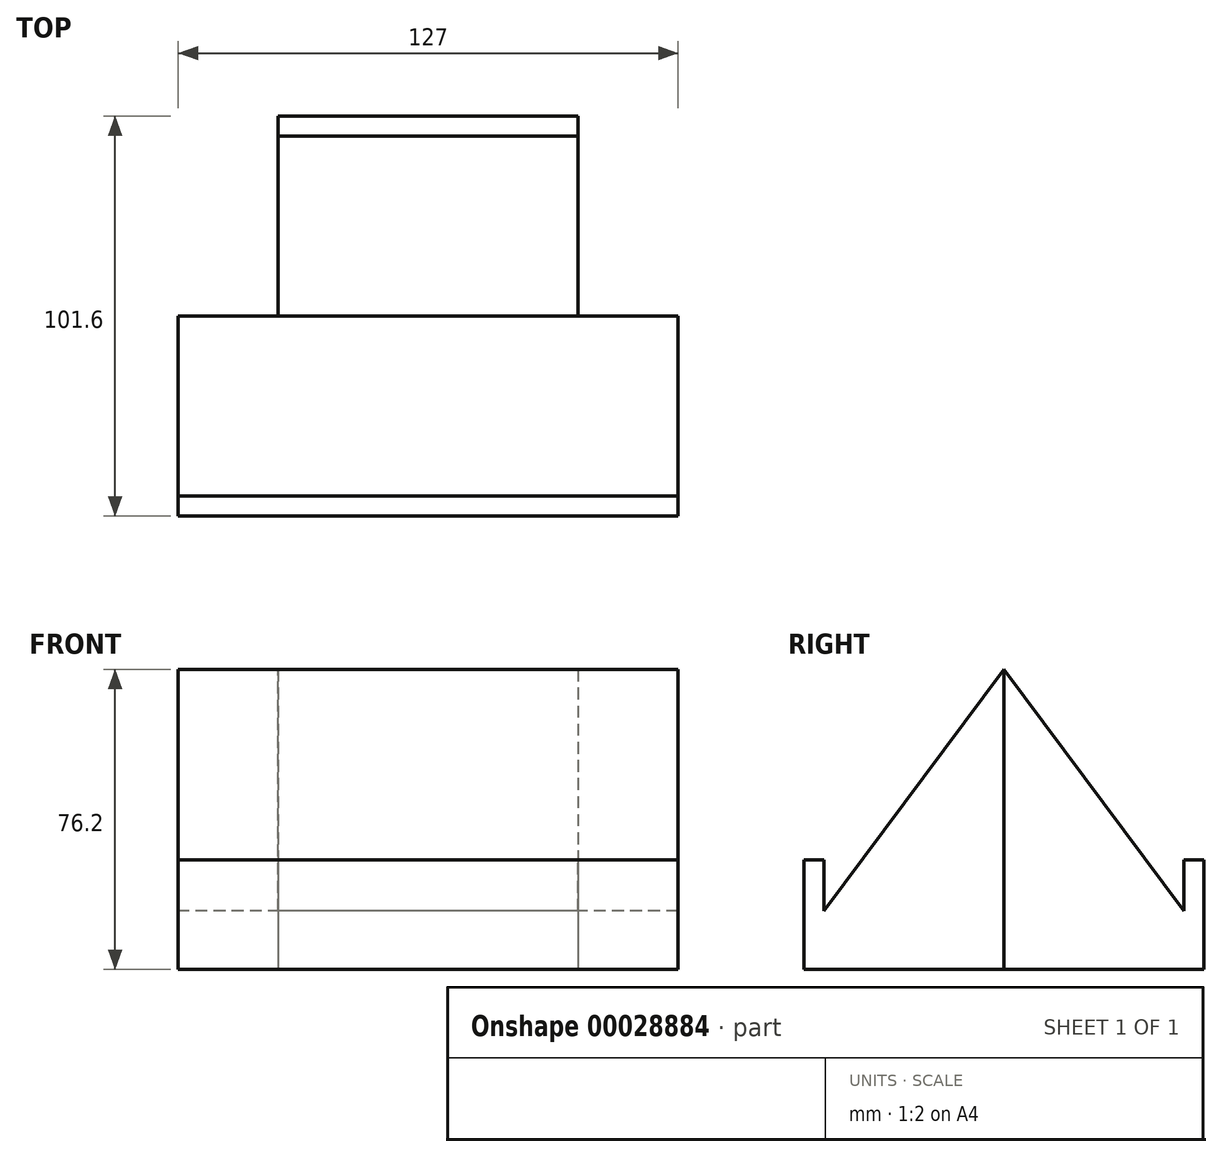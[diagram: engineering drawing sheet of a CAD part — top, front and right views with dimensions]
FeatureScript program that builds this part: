
annotation { "Feature Type Name" : "Feature", "Feature Type Description" : "" }
export const myFeature = defineFeature(function(context is Context, id is Id, definition is map)
    precondition{}
    {
        {
            var Q0;
            Q0=qCreatedBy(makeId("Front.planeOp"),FACE);
            var sketch = newSketch(context, id + "F0", { "sketchPlane" : qUnion([Q0])});
            skLineSegment(sketch, "E0.bottom", {"start": v(-63.5, 32.59) * mm, "end": v(63.5, 32.59) * mm});
            skLineSegment(sketch, "E0.top", {"start": v(-63.5, -43.61) * mm, "end": v(63.5, -43.61) * mm});
            skLineSegment(sketch, "E0.left", {"start": v(-63.5, 32.59) * mm, "end": v(-63.5, -43.61) * mm});
            skLineSegment(sketch, "E0.right", {"start": v(63.5, 32.59) * mm, "end": v(63.5, -43.61) * mm});
            skSolve(sketch);
        }
        {
            var Q0;
            Q0 = qSketchRegion(id + "F0", true);
            extrude(context, id + "F1", {"entities" : qUnion([Q0]), "oppositeDirection" : true, "depth" : 25.4 * mm});
        }
        {
            var Q0;
            Q0=makeQuery(id+"F1.opExtrude","CAP_FACE",FACE,{"disambiguationData":[OSD([sQuery(id+"F0.wireOp",EDGE,"E0.bottom"),sQuery(id+"F0.wireOp",EDGE,"E0.top"),sQuery(id+"F0.wireOp",EDGE,"E0.left"),sQuery(id+"F0.wireOp",EDGE,"E0.right")])],"isStart":true});
            extrude(context, id + "F2", {"entities" : qUnion([Q0]), "operationType" : NewBodyOperationType.ADD, "depth" : 25.4 * mm});
        }
        {
            var Q0;
            Q0=makeQuery(id+"F2.opExtrude","CAP_FACE",FACE,{"disambiguationData":[OSD([sQuery(id+"F0.wireOp",EDGE,"E0.bottom"),sQuery(id+"F0.wireOp",EDGE,"E0.top"),sQuery(id+"F0.wireOp",EDGE,"E0.left"),sQuery(id+"F0.wireOp",EDGE,"E0.right")])],"isStart":false});
            var sketch = newSketch(context, id + "F3", { "sketchPlane" : qUnion([Q0])});
            skLineSegment(sketch, "E1.bottom", {"start": v(-63.5, 32.59) * mm, "end": v(63.5, 32.59) * mm});
            skLineSegment(sketch, "E1.top", {"start": v(-63.5, -22.16) * mm, "end": v(63.5, -22.16) * mm});
            skLineSegment(sketch, "E1.left", {"start": v(-63.5, 32.59) * mm, "end": v(-63.5, -22.16) * mm});
            skLineSegment(sketch, "E1.right", {"start": v(63.5, 32.59) * mm, "end": v(63.5, -22.16) * mm});
            skSolve(sketch);
        }
        {
            var Q0;
            Q0 = qSketchRegion(id + "F3", true);
            extrude(context, id + "F4", {"entities" : qUnion([Q0]), "operationType" : NewBodyOperationType.REMOVE, "oppositeDirection" : true, "depth" : 5.08 * mm});
        }
        {
            var Q0;
            {var subQ0=sQuery(id+"F0.wireOp",EDGE,"E0.left");Q0=makeQuery(id+"F2.boolean.opBoolean","MERGE",FACE,{"derivedFrom":[makeQuery(id+"F1.opExtrude","SWEPT_FACE",FACE,{"disambiguationData":[OSD([subQ0])]}),makeQuery(id+"F2.opExtrude","SWEPT_FACE",FACE,{"disambiguationData":[OSD([subQ0])]})]});}
            var sketch = newSketch(context, id + "F5", { "sketchPlane" : qUnion([Q0])});
            skLineSegment(sketch, "E2", {"start": v(-25.4, 32.59) * mm, "end": v(20.32, 32.59) * mm});
            skLineSegment(sketch, "E3", {"start": v(20.32, 32.59) * mm, "end": v(20.32, -28.71) * mm});
            skLineSegment(sketch, "E4", {"start": v(20.32, -28.71) * mm, "end": v(-25.4, 32.59) * mm});
            skSolve(sketch);
        }
        {
            var Q0;
            Q0 = qSketchRegion(id + "F5", true);
            extrude(context, id + "F6", {"entities" : qUnion([Q0]), "operationType" : NewBodyOperationType.REMOVE, "oppositeDirection" : true, "depth" : 129.54 * mm});
        }
        {
            var Q0;
            Q0=makeQuery(id+"F4.boolean.opBoolean","COPY",FACE,{"derivedFrom":makeQuery(id+"F4.opExtrude","SWEPT_FACE",FACE,{"disambiguationData":[OSD([sQuery(id+"F3.wireOp",EDGE,"E1.top")])]})});
            extrude(context, id + "F7", {"entities" : qUnion([Q0]), "operationType" : NewBodyOperationType.ADD, "depth" : 6.35 * mm});
        }
        {
            var Q0;
            Q0=makeQuery(id+"F1.opExtrude","SWEPT_BODY",BODY,{"disambiguationData":[OSD([sQuery(id+"F0.wireOp",EDGE,"E0.bottom"),sQuery(id+"F0.wireOp",EDGE,"E0.top"),sQuery(id+"F0.wireOp",EDGE,"E0.left"),sQuery(id+"F0.wireOp",EDGE,"E0.right")])]});
            var Q1;
            Q1=makeQuery(id+"F1.opExtrude","CAP_FACE",FACE,{"disambiguationData":[OSD([sQuery(id+"F0.wireOp",EDGE,"E0.bottom"),sQuery(id+"F0.wireOp",EDGE,"E0.top"),sQuery(id+"F0.wireOp",EDGE,"E0.left"),sQuery(id+"F0.wireOp",EDGE,"E0.right")])],"isStart":false});
            mirror(context, id + "F8", {"operationType" : NewBodyOperationType.ADD, "entities" : qUnion([Q0]), "mirrorPlane" : qUnion([Q1])});
        }
        {
            var Q0;
            {var subQ0=sQuery(id+"F0.wireOp",EDGE,"E0.right");var subQ1=makeQuery(id+"F7.boolean.opBoolean","MERGE",FACE,{"derivedFrom":[makeQuery(id+"F2.boolean.opBoolean","MERGE",FACE,{"derivedFrom":[makeQuery(id+"F1.opExtrude","SWEPT_FACE",FACE,{"disambiguationData":[OSD([subQ0])]}),makeQuery(id+"F2.opExtrude","SWEPT_FACE",FACE,{"disambiguationData":[OSD([subQ0])]})]}),makeQuery(id+"F7.opExtrude","SWEPT_FACE",FACE,{"disambiguationData":[OSD([subQ0,sQuery(id+"F3.wireOp",EDGE,"E1.top"),sQuery(id+"F3.wireOp",EDGE,"E1.right")])]})]});Q0=makeQuery(id+"F8.boolean.opBoolean","MERGE",FACE,{"derivedFrom":[subQ1,makeQuery(id+"F8.opPattern","COPY",FACE,{"derivedFrom":subQ1,"instanceName":"1"})]});}
            var sketch = newSketch(context, id + "F9", { "sketchPlane" : qUnion([Q0])});
            skLineSegment(sketch, "E5.bottom", {"start": v(25.4, 32.59) * mm, "end": v(76.2, 32.59) * mm});
            skLineSegment(sketch, "E5.top", {"start": v(25.4, -43.61) * mm, "end": v(76.2, -43.61) * mm});
            skLineSegment(sketch, "E5.left", {"start": v(25.4, 32.59) * mm, "end": v(25.4, -43.61) * mm});
            skLineSegment(sketch, "E5.right", {"start": v(76.2, 32.59) * mm, "end": v(76.2, -43.61) * mm});
            skSolve(sketch);
        }
        {
            var Q0;
            Q0 = qSketchRegion(id + "F9", true);
            extrude(context, id + "F10", {"entities" : qUnion([Q0]), "operationType" : NewBodyOperationType.REMOVE, "oppositeDirection" : true, "depth" : 25.4 * mm});
        }
        {
            var Q0;
            {var subQ0=sQuery(id+"F0.wireOp",EDGE,"E0.left");var subQ1=makeQuery(id+"F7.boolean.opBoolean","MERGE",FACE,{"derivedFrom":[makeQuery(id+"F2.boolean.opBoolean","MERGE",FACE,{"derivedFrom":[makeQuery(id+"F1.opExtrude","SWEPT_FACE",FACE,{"disambiguationData":[OSD([subQ0])]}),makeQuery(id+"F2.opExtrude","SWEPT_FACE",FACE,{"disambiguationData":[OSD([subQ0])]})]}),makeQuery(id+"F7.opExtrude","SWEPT_FACE",FACE,{"disambiguationData":[OSD([subQ0,sQuery(id+"F3.wireOp",EDGE,"E1.top"),sQuery(id+"F3.wireOp",EDGE,"E1.left")])]})]});Q0=makeQuery(id+"F8.boolean.opBoolean","MERGE",FACE,{"derivedFrom":[subQ1,makeQuery(id+"F8.opPattern","COPY",FACE,{"derivedFrom":subQ1,"instanceName":"1"})]});}
            var sketch = newSketch(context, id + "F11", { "sketchPlane" : qUnion([Q0])});
            skLineSegment(sketch, "E6.bottom", {"start": v(-25.4, 32.59) * mm, "end": v(-76.2, 32.59) * mm});
            skLineSegment(sketch, "E6.top", {"start": v(-25.4, -43.61) * mm, "end": v(-76.2, -43.61) * mm});
            skLineSegment(sketch, "E6.left", {"start": v(-25.4, 32.59) * mm, "end": v(-25.4, -43.61) * mm});
            skLineSegment(sketch, "E6.right", {"start": v(-76.2, 32.59) * mm, "end": v(-76.2, -43.61) * mm});
            skSolve(sketch);
        }
        {
            var Q0;
            Q0 = qSketchRegion(id + "F11", true);
            extrude(context, id + "F12", {"entities" : qUnion([Q0]), "operationType" : NewBodyOperationType.REMOVE, "oppositeDirection" : true, "depth" : 25.4 * mm});
        }
    });
